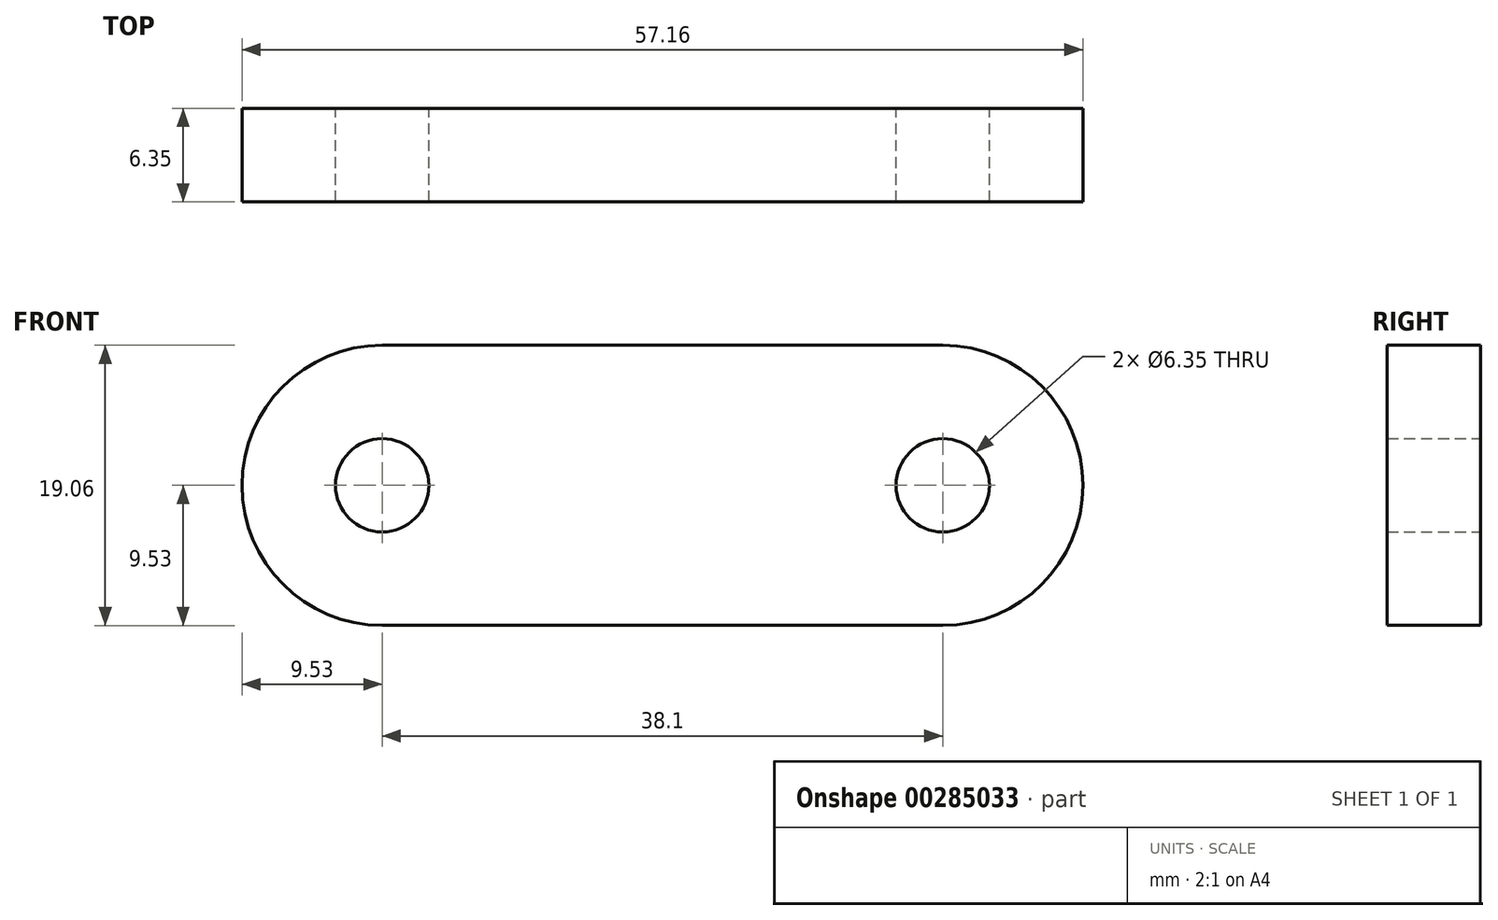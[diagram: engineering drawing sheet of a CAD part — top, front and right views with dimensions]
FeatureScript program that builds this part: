
annotation { "Feature Type Name" : "Feature", "Feature Type Description" : "" }
export const myFeature = defineFeature(function(context is Context, id is Id, definition is map)
    precondition{}
    {
        {
            var Q0;
            Q0=qCreatedBy(makeId("Front.planeOp"),FACE);
            var sketch = newSketch(context, id + "F0", { "sketchPlane" : qUnion([Q0])});
            skLineSegment(sketch, "E0.bottom", {"start": v(19.05, -9.52) * mm, "end": v(-19.05, -9.53) * mm});
            skLineSegment(sketch, "E0.top", {"start": v(19.05, 9.53) * mm, "end": v(-19.05, 9.52) * mm});
            skPoint(sketch, "E0.middle", {"position": v(0, 0) * mm});
            skArc(sketch, "E1", {"start": v(-19.05, 9.52) * mm, "mid": v(-28.58, 0) * mm, "end": v(-19.05, -9.53) * mm});
            skArc(sketch, "E2", {"start": v(19.05, -9.52) * mm, "mid": v(28.58, 0) * mm, "end": v(19.05, 9.53) * mm});
            skCircle(sketch, "E3", {"center": v(-19.05, 0) * mm, "radius": 3.18 * mm});
            skCircle(sketch, "E4", {"center": v(19.05, 0) * mm, "radius": 3.18 * mm});
            skSolve(sketch);
        }
        {
            var Q0;
            Q0 = qSketchRegion(id + "F0", true);
            extrude(context, id + "F1", {"entities" : qUnion([Q0]), "depth" : 6.35 * mm});
        }
    });
